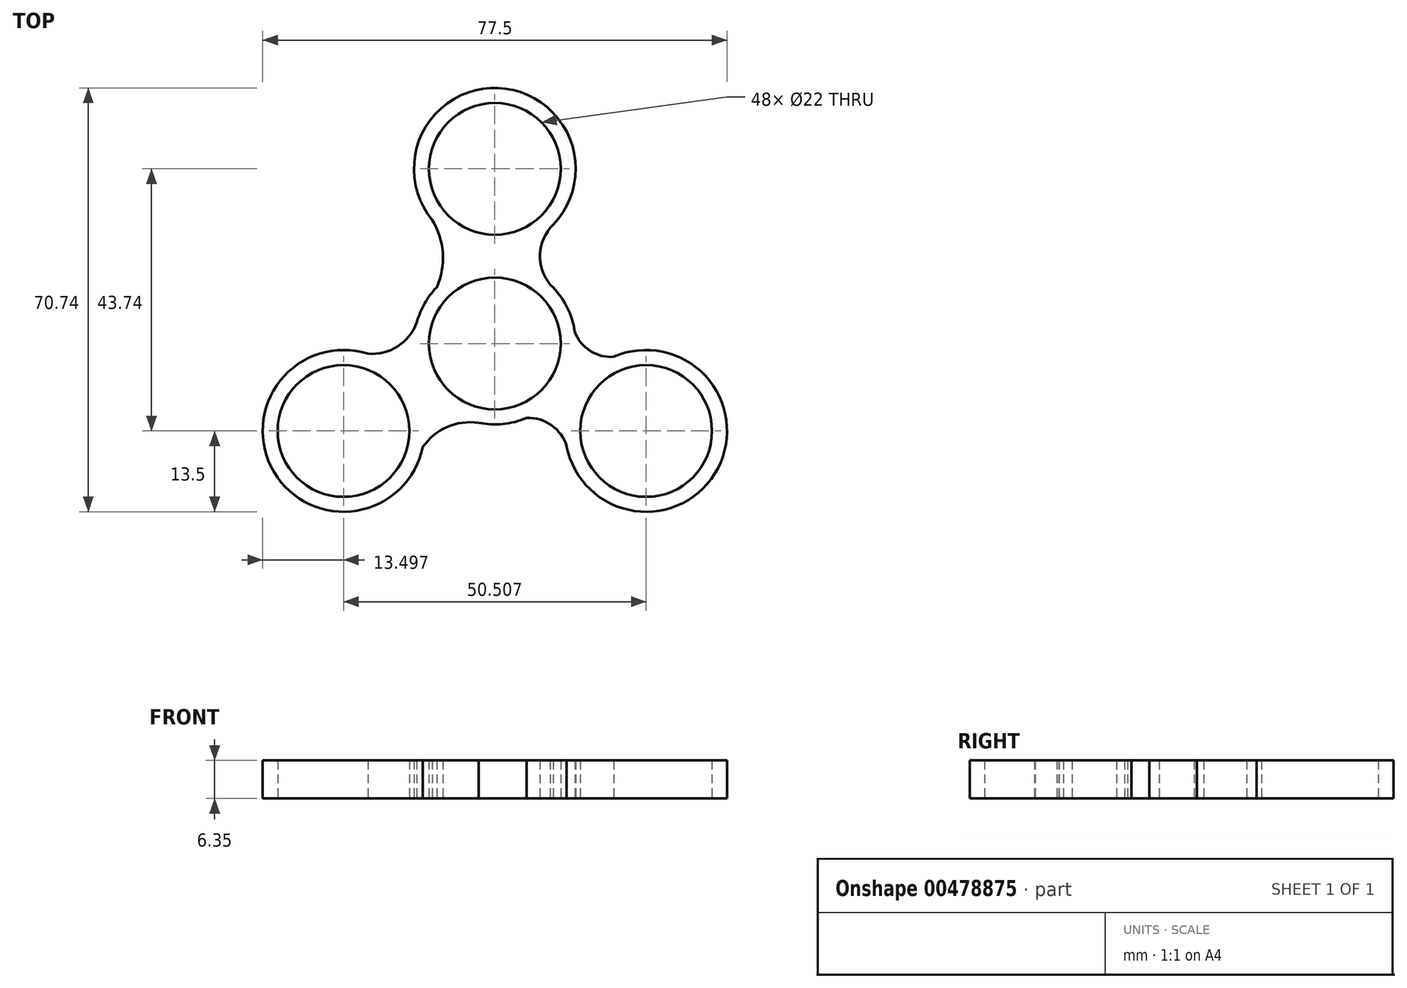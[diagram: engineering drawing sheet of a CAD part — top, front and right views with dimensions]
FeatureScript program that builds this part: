
annotation { "Feature Type Name" : "Feature", "Feature Type Description" : "" }
export const myFeature = defineFeature(function(context is Context, id is Id, definition is map)
    precondition{}
    {
        {
            var Q0;
            Q0=qCreatedBy(makeId("Top.planeOp"),FACE);
            var sketch = newSketch(context, id + "F0", { "sketchPlane" : qUnion([Q0])});
            skCircle(sketch, "E0", {"center": v(0, 0) * mm, "radius": 11 * mm});
            skCircle(sketch, "E1", {"center": v(0, 0) * mm, "radius": 13.5 * mm});
            skCircle(sketch, "E2", {"center": v(0, 29.16) * mm, "radius": 11 * mm});
            skCircle(sketch, "E3", {"center": v(0, 29.16) * mm, "radius": 13.5 * mm});
            skCircle(sketch, "E4.1.0", {"center": v(-25.25, -14.58) * mm, "radius": 11 * mm});
            skCircle(sketch, "E4.2.0", {"center": v(25.25, -14.58) * mm, "radius": 11 * mm});
            skCircle(sketch, "E5.1.0", {"center": v(-25.25, -14.58) * mm, "radius": 13.5 * mm});
            skCircle(sketch, "E5.2.0", {"center": v(25.25, -14.58) * mm, "radius": 13.5 * mm});
            skArc(sketch, "E6", {"start": v(-9.69, 9.4) * mm, "mid": v(-8.68, 15.1) * mm, "end": v(-10.44, 20.6) * mm});
            skArc(sketch, "E7", {"start": v(9.76, 19.84) * mm, "mid": v(7.53, 14.92) * mm, "end": v(9.27, 9.81) * mm});
            skArc(sketch, "E8", {"start": v(-21.2, -1.7) * mm, "mid": v(-16.22, -0.47) * mm, "end": v(-13.03, 3.55) * mm});
            skArc(sketch, "E9", {"start": v(-2.71, -13.22) * mm, "mid": v(-7.94, -13.91) * mm, "end": v(-12.02, -17.25) * mm});
            skArc(sketch, "E10", {"start": v(12, -17.17) * mm, "mid": v(9.46, -13.64) * mm, "end": v(5.28, -12.43) * mm});
            skArc(sketch, "E11", {"start": v(13.36, 1.91) * mm, "mid": v(15.92, -1.22) * mm, "end": v(19.84, -2.21) * mm});
            skSolve(sketch);
        }
        {
            var Q0;
            Q0=makeQuery(id+"F0.imprint","IMPRINT",FACE,{"disambiguationData":[TD([[makeQuery(id+"F0.imprint","IMPRINT",EDGE,{"derivedFrom":sQuery(id+"F0.wireOp",EDGE,"E2")}),-1.0]])]});
            var Q1;
            Q1=makeQuery(id+"F0.imprint","IMPRINT",FACE,{"disambiguationData":[TD([[makeQuery(id+"F0.imprint","IMPRINT",EDGE,{"derivedFrom":sQuery(id+"F0.wireOp",EDGE,"E0")}),-1.0]])]});
            var Q2;
            Q2=makeQuery(id+"F0.imprint","IMPRINT",FACE,{"disambiguationData":[TD([[makeQuery(id+"F0.imprint","IMPRINT",EDGE,{"derivedFrom":sQuery(id+"F0.wireOp",EDGE,"E4.1.0")}),-1.0]])]});
            var Q3;
            Q3=makeQuery(id+"F0.imprint","IMPRINT",FACE,{"disambiguationData":[TD([[makeQuery(id+"F0.imprint","IMPRINT",EDGE,{"derivedFrom":sQuery(id+"F0.wireOp",EDGE,"E4.2.0")}),-1.0]])]});
            var Q4;
            {var subQ0=sQuery(id+"F0.wireOp",EDGE,"E10");Q4=makeQuery(id+"F0.imprint","IMPRINT",FACE,{"disambiguationData":[TD([[makeQuery(id+"F0.imprint","IMPRINT",EDGE,{"derivedFrom":subQ0}),-1.0]])]});}
            var Q5;
            {var subQ0=sQuery(id+"F0.wireOp",EDGE,"E8");Q5=makeQuery(id+"F0.imprint","IMPRINT",FACE,{"disambiguationData":[TD([[makeQuery(id+"F0.imprint","IMPRINT",EDGE,{"derivedFrom":subQ0}),-1.0]])]});}
            var Q6;
            {var subQ0=sQuery(id+"F0.wireOp",EDGE,"E6");Q6=makeQuery(id+"F0.imprint","IMPRINT",FACE,{"disambiguationData":[TD([[makeQuery(id+"F0.imprint","IMPRINT",EDGE,{"derivedFrom":subQ0}),-1.0]])]});}
            extrude(context, id + "F1", {"entities" : qUnion([Q0, Q1, Q2, Q3, Q4, Q5, Q6]), "depth" : 6.35 * mm});
        }
    });
